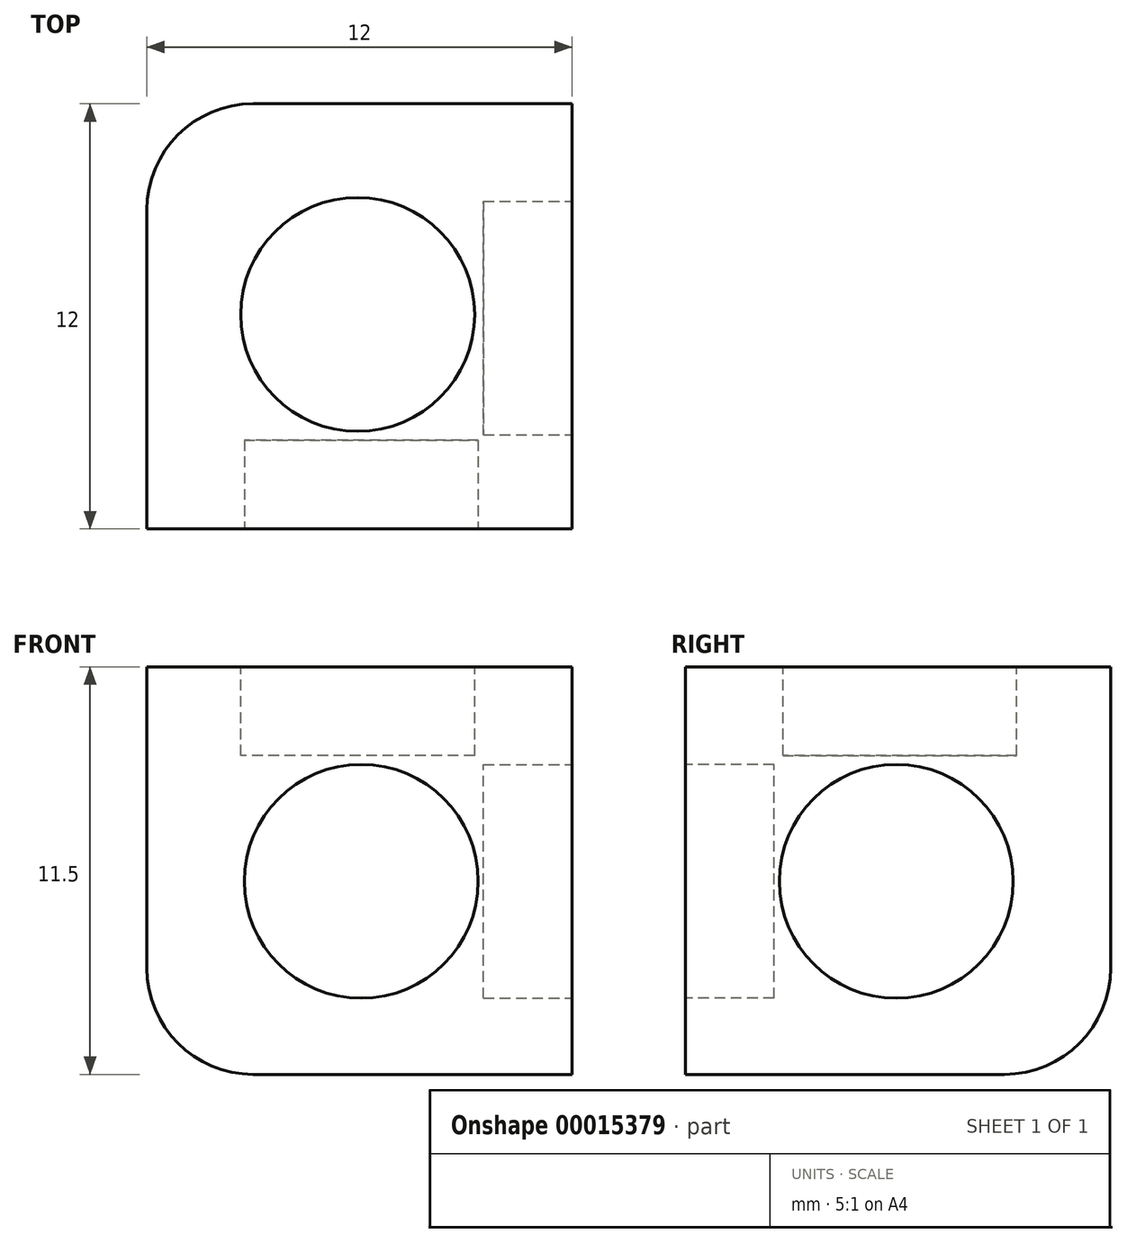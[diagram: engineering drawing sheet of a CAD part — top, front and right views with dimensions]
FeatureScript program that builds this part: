
annotation { "Feature Type Name" : "Feature", "Feature Type Description" : "" }
export const myFeature = defineFeature(function(context is Context, id is Id, definition is map)
    precondition{}
    {
        {
            var Q0;
            Q0=qCreatedBy(makeId("Top.planeOp"),FACE);
            var sketch = newSketch(context, id + "F0", { "sketchPlane" : qUnion([Q0])});
            skLineSegment(sketch, "E0.bottom", {"start": v(6, 6) * mm, "end": v(-6, 6) * mm});
            skLineSegment(sketch, "E0.top", {"start": v(6, -6) * mm, "end": v(-6, -6) * mm});
            skLineSegment(sketch, "E0.left", {"start": v(6, 6) * mm, "end": v(6, -6) * mm});
            skLineSegment(sketch, "E0.right", {"start": v(-6, 6) * mm, "end": v(-6, -6) * mm});
            skSolve(sketch);
        }
        {
            var Q0;
            Q0=qSketchRegion(id+"F0",true);
            extrude(context, id + "F1", {"entities" : qUnion([Q0]), "oppositeDirection" : true, "depth" : 11.5 * mm});
        }
        {
            var Q0;
            Q0=makeQuery(id+"F1.opExtrude","CAP_FACE",FACE,{"disambiguationData":[OSD([sQuery(id+"F0.wireOp",EDGE,"E0.bottom"),sQuery(id+"F0.wireOp",EDGE,"E0.top"),sQuery(id+"F0.wireOp",EDGE,"E0.left"),sQuery(id+"F0.wireOp",EDGE,"E0.right")])],"isStart":true});
            var sketch = newSketch(context, id + "F2", { "sketchPlane" : qUnion([Q0])});
            skCircle(sketch, "E1", {"center": v(-0.05, 0.05) * mm, "radius": 3.3 * mm});
            skSolve(sketch);
        }
        {
            var Q0;
            Q0=qSketchRegion(id+"F2",true);
            extrude(context, id + "F3", {"entities" : qUnion([Q0]), "operationType" : NewBodyOperationType.REMOVE, "oppositeDirection" : true, "depth" : 2.5 * mm});
        }
        {
            var Q0;
            Q0=makeQuery(id+"F1.opExtrude","SWEPT_FACE",FACE,{"disambiguationData":[OSD([sQuery(id+"F0.wireOp",EDGE,"E0.top")])]});
            var sketch = newSketch(context, id + "F4", { "sketchPlane" : qUnion([Q0])});
            skCircle(sketch, "E2", {"center": v(0.05, -6.05) * mm, "radius": 3.3 * mm});
            skSolve(sketch);
        }
        {
            var Q0;
            Q0=qSketchRegion(id+"F4",true);
            extrude(context, id + "F5", {"entities" : qUnion([Q0]), "operationType" : NewBodyOperationType.REMOVE, "oppositeDirection" : true, "depth" : 2.5 * mm});
        }
        {
            var Q0;
            Q0=makeQuery(id+"F1.opExtrude","SWEPT_FACE",FACE,{"disambiguationData":[OSD([sQuery(id+"F0.wireOp",EDGE,"E0.left")])]});
            var sketch = newSketch(context, id + "F6", { "sketchPlane" : qUnion([Q0])});
            skCircle(sketch, "E3", {"center": v(-0.05, -6.05) * mm, "radius": 3.3 * mm});
            skSolve(sketch);
        }
        {
            var Q0;
            Q0=qSketchRegion(id+"F6",true);
            extrude(context, id + "F7", {"entities" : qUnion([Q0]), "operationType" : NewBodyOperationType.REMOVE, "oppositeDirection" : true, "depth" : 2.5 * mm});
        }
        {
            var Q0;
            Q0=makeQuery(id+"F1.opExtrude","CAP_EDGE",EDGE,{"disambiguationData":[OSD([sQuery(id+"F0.wireOp",EDGE,"E0.bottom")])],"isStart":false});
            var Q1;
            Q1=makeQuery(id+"F1.opExtrude","SWEPT_EDGE",EDGE,{"disambiguationData":[OSD([sQuery(id+"F0.wireOp",EDGE,"E0.bottom"),sQuery(id+"F0.wireOp",EDGE,"E0.right")])]});
            var Q2;
            Q2=makeQuery(id+"F1.opExtrude","CAP_EDGE",EDGE,{"disambiguationData":[OSD([sQuery(id+"F0.wireOp",EDGE,"E0.right")])],"isStart":false});
            fillet(context, id + "F8", {"entities" : qUnion([Q0, Q1, Q2]), "radius" : 3 * mm, "tangentPropagation" : true, "allowEdgeOverflow" : false});
        }
    });
